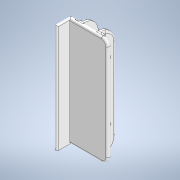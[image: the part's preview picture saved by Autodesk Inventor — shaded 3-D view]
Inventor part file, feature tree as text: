
AUTODESK INVENTOR PART (.ipt)
format: ipt  version: 2020.3 (Build 243373000, 373)  size: 299,008 bytes
history: native  units: mm
features: fillet x5, sketch x4, extrude x3, other x1, hole x1
ambient origin geometry x8: Origin, YZ Plane, XZ Plane, XY Plane, X Axis, Y Axis, Z Axis, Center Point
bodies: Body1 (feature_tree)
feature tree (14):
  other  "ソリッド1"
  extrude  "押し出し1"  Depth=32.0mm
  extrude  "押し出し2"  Depth=86.0mm
  extrude  "押し出し3"  Depth=3.0mm TaperAngle=0.0deg
  fillet  "フィレット1"  Radius=30.0mm
  fillet  "フィレット2"  Radius=10.0mm
  fillet  "フィレット3"  Radius=11.0mm
  fillet  "フィレット4"  Radius=3.0mm
  fillet  "フィレット5"  Radius=3.0mm
  hole  "穴1"  [1 undecoded]
  sketch  "スケッチ1"
  sketch  "スケッチ2"
  sketch  "スケッチ3"
  sketch  "スケッチ4"
note: 1 required parameter value undecoded (feature->parameter linkage not recoverable at this tier; creation-order binding heuristic only, values carry confidence <= 0.55)
